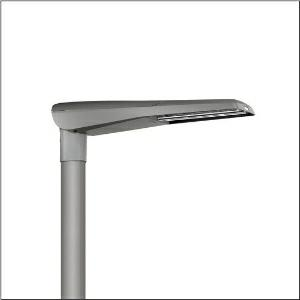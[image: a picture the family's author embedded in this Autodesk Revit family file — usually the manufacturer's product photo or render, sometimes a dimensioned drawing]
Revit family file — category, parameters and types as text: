
# Revit family: streetlight_sl_11_iq_mini___st1_0ab_5xc2nc1f08ge_aec6
name_source: partatom
category: Lighting Fixtures
units: mm (PartAtom-declared; Revit-internal decimal feet)

## family parameters
Cut with Voids When Loaded = No
Host = Face
Light Source = No
Part Type = Normal
Room Calculation Point = No
Round Connector Dimension = Use Diameter
Shared = No

## types (1)
- --- (1 x LED, 2430 lm, 25.3 W, 2200K)
    Apparent Load = 25 VA
    CIE Flux Codes = 29 63 95 100 100
    Color Rendering = 70
    Color Temperature = 2200K
    Default Elevation = 1800 mm
    Description = Streetlight SL 11 iQ mini, mast luminaire, primary light control with 3 zone facetted reflector, of plastic, silver coated, highly specular, primary optical cover: cover, of PMMA, transparent, light distribution: ST1.0aB, light emission: direct distribution, primary light characteristic: asymmetric, installation type: post-top, side-entry, lamps: LED, High Power LED, rated values: 2.860lm | 24,9W | 114,9lm/W (begin service life); end service life: 2.860lm | 25,7W; at 50% lumin. flux: 1.430lm | 12,8W | 111,7lm/W, colour temperature: 2200/2700/3000/4000K, colour rendering: CRI > 70, light colour: 722/727/730/740, light setting 1 begin service life: 100% | 2.860lm | 24,9W | 114,9lm/W | 3.000K, light setting 1 end service life: 25,7W, further light settings possible, control: Street-Remote, Auto-Match, Temp-Guard, Lumen-Switch, Night-Set, Smart-Wire, Light-Fading, Desk-Remote (wireless, voltage-free reading and setting of iQ features in the workshop via application-optimized NFC function/RFID function), optimised constant luminous flux control (CLO 2.0), with cable H07RN-F 3x 1.5mm², mains connection: 230..240V, AC, 50/60Hz, connection cable pre-assembled, cable length: 6,5m, luminaire housing, of diecast aluminium, powder-coated, SITECO metallic grey (DB 702S), please order mast flange separately, inclination adjustable without tools: 0°, 5°, 10°, 15° (post-top) | 0°, -5°, -10°, -15° (side-entry), sealing non-destructively replaceable, multi-level sealing system, length: 736mm, width: 174mm, height: 116mm, mast flange for spigot size: 42mm (side-entry): 5XC10008XM4, 60/48mm (side-entry/post-top): 5XC10108XM2, 76/60mm (side-entry/post-top): 5XC10108XM1, equipment: standard, protection rating (complete): IP66, insulation class (complete): insulation class II (safety insulation), certification: CE, ENEC, ENEC+, VDE, impact resistance: IK10, permissible operating ambient temperature for outdoor applications: -25..+50°C, standard-compliant lighting for roads and squares, Environmental Product Declaration (EPD) tested and certified by an independent institute, packaging unit: 1 piece

Light Distribution: ST1.0aB
    Height = 116 mm
    Lamp = 1 x LED
    Lamp Light Flux = 2430 lm
    Lamp Power = 25.3 W
    Lamp count = 1
    Length = 736 mm
    Luminous efficacy = 96 lm/W
    Manufacturer = Siteco
    ModVariant = No
    Model = 5XC2NC1F08GE
    Number of Poles = 1
    OnlyDefault = Yes
    Power Factor = 1
    Product Name = Streetlight SL 11 iQ mini | ST1.0aB
    Product group = mast luminaire | pylon top
    ProductGroupID = 6100
    Protection Class = Protection class II
    Protection Degree = IP 66
    RLX_Detail_Level = 1
    RLX_Emergency_Light_Flux = 0 lm
    RLX_Emergency_Type = 0
    RLX_Emergency_Type_DB = No
    RlxData = <blob elided: 52821 chars, md5=829e7a41>
    Socket = socket
    Standby Power = 0 W
    System Light Flux = 2430 lm
    System Power = 25 W
    Type Comments = individual setting: luminous flux: 100 % | dim-lin: 254 | 351 mA
    Type Image = l_1003508.jpg
    URL = http://relux.com
    VarID = @adj_021271
    Voltage = 0 V
    Weight = 0.00 kg
    Width = 174 mm

## geometry (parser evidence)
native form markers: Blend x4, Sweep x9
no freeform markers — native parametric forms only
